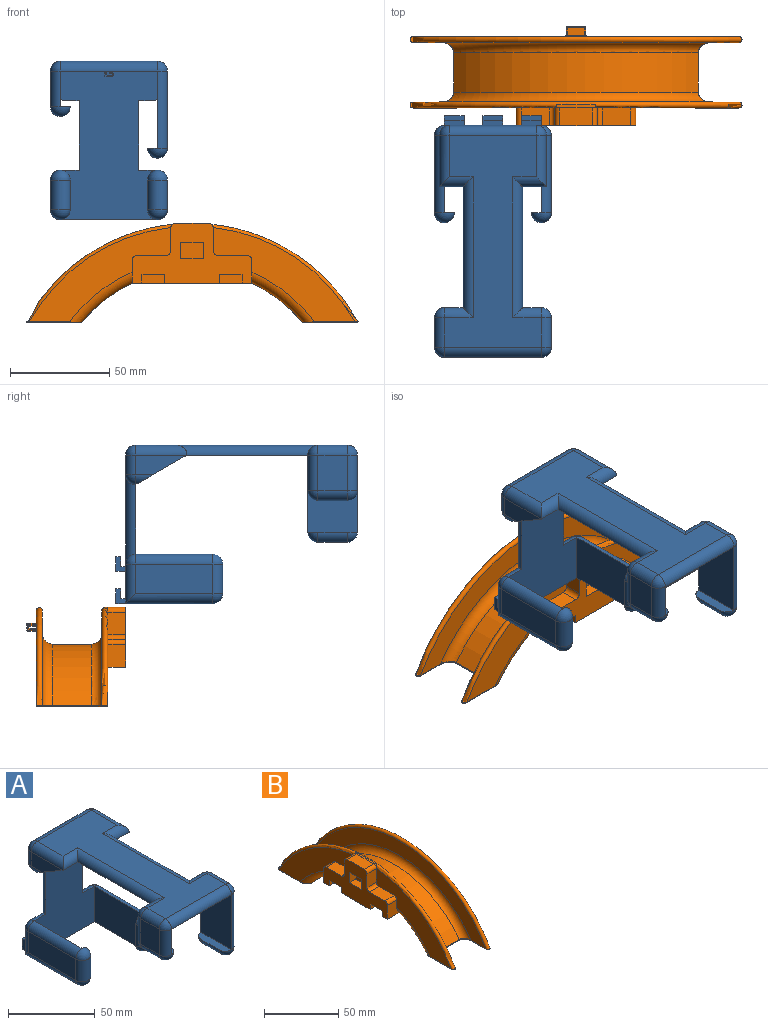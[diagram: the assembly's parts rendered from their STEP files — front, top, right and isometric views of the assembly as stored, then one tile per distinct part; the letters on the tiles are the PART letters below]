
ASSEMBLY  parts=2 mates=1
PART A: 174 faces, bbox 59x122x80 mm
  f0: plane 75x49mm, normal (0,-1,0), area 3005.6mm2, adj f8,f19,f20,f24,f27,f28,f47,f50
  f1: plane 10x2.5mm, normal (0,0,1), area 25mm2, adj f2,f87,f89,f95
  f2: plane 7.5x5mm, normal (1,0,0), area 25mm2, adj f1,f5,f88,f89,f94,f95
  f3: plane 10x2.5mm, normal (0,0,1), area 25mm2, adj f4,f81,f82,f93
  f4: plane 7.5x5mm, normal (1,0,0), area 25mm2, adj f3,f24,f38,f82,f92,f93
  f5: plane 75x49mm, normal (0,1,0), area 2245mm2, adj f2,f24,f38,f47,f50,f54,f61,f66
  f6: plane 25x5mm, normal (0,0,1), area 114.3mm2, adj f7,f15,f35,f41
  f7: plane 25x18mm, normal (1,0,0), area 450mm2, adj f6,f8,f46,f53
  f8: plane 112x49mm, normal (0,0,-1), area 4328.6mm2, adj f0,f7,f9,f27,f28,f45,f51,f56
  f9: plane 39x25mm, normal (-1,0,0), area 975mm2, adj f8,f10,f37,f43
  f10: plane 25x5mm, normal (0,0,1), area 114.3mm2, adj f9,f11,f32,f34
  f11: cylinder r=5mm len=15mm, axis (0,-1,0), area 235.6mm2, adj f10,f12,f32,f34
  f12: plane 39x15mm, normal (1,0,0), area 585mm2, adj f11,f37,f43,f44
  f13: plane 107x49mm, normal (0,0,1), area 3078.5mm2, adj f44,f45,f51,f52,f56,f59,f60,f62
  f14: plane 18x15mm, normal (-1,0,0), area 270mm2, adj f15,f46,f52,f53
  f15: cylinder r=5mm len=15mm, axis (0,-1,0), area 235.6mm2, adj f6,f14,f35,f41
  f16: plane 39x15mm, normal (1,0,0), area 585mm2, adj f17,f36,f38,f39
  f17: cylinder r=5mm len=15mm, axis (0,0,1), area 235.6mm2, adj f16,f18,f31,f33
  f18: plane 25x5mm, normal (0,1,0), area 114.3mm2, adj f17,f19,f31,f33
  f19: plane 39x25mm, normal (-1,0,0), area 975mm2, adj f0,f18,f36,f39
  f20: plane 39x25mm, normal (1,0,0), area 975mm2, adj f0,f21,f75,f79
  f21: plane 25x5mm, normal (0,1,0), area 114.3mm2, adj f20,f22,f73,f80
  f22: cylinder r=5mm len=15mm, axis (0,0,1), area 235.6mm2, adj f21,f23,f73,f80
  f23: plane 39x15mm, normal (-1,0,0), area 585mm2, adj f22,f75,f76,f79
  f24: plane 49x10mm, normal (0,0,-1), area 345mm2, adj f0,f4,f5,f36,f75,f81,f82,f83
  f25: plane 24.82x14.33mm, normal (0,-0.5,-0.87), area 65.4mm2, adj f26,f27,f55,f59
  f26: plane 25.98x10mm, normal (1,0,0), area 173.2mm2, adj f25,f55,f61,f62
  f27: plane 25.98x14.33mm, normal (-1,0,0), area 194.5mm2, adj f0,f8,f25,f55
  f28: plane 25.98x14.33mm, normal (1,0,0), area 194.5mm2, adj f0,f8,f29,f70
  f29: plane 24.82x14.33mm, normal (0,-0.5,-0.87), area 65.4mm2, adj f28,f30,f65,f70
  f30: plane 25.98x10mm, normal (-1,0,0), area 173.2mm2, adj f29,f67,f69,f70
  f31: sphere r=5mm, area 78.5mm2, adj f17,f18,f36
  f32: sphere r=5mm, area 78.5mm2, adj f10,f11,f37
  f33: sphere r=5mm, area 78.5mm2, adj f17,f18,f39
  f34: sphere r=5mm, area 78.5mm2, adj f10,f11,f43
  f35: sphere r=5mm, area 78.5mm2, adj f6,f15,f46
  f36: cylinder r=5mm len=44mm, axis (0,1,0), area 331.3mm2, adj f16,f19,f24,f31,f38
  f37: cylinder r=5mm len=39mm, axis (0,0,1), area 306.3mm2, adj f9,f12,f32,f40
  f38: cylinder r=5mm len=20mm, axis (0,0,-1), area 142.8mm2, adj f4,f5,f16,f36,f42
  f39: cylinder r=5mm len=39mm, axis (0,-1,0), area 306.3mm2, adj f16,f19,f33,f42
  f40: sphere r=5mm, area 39.3mm2, adj f37,f44,f45
  f41: sphere r=5mm, area 78.5mm2, adj f6,f15,f53
  f42: sphere r=5mm, area 39.3mm2, adj f38,f39,f47
  f43: cylinder r=5mm len=39mm, axis (0,0,-1), area 306.3mm2, adj f9,f12,f34,f48
  f44: cylinder r=5mm len=15mm, axis (0,-1,0), area 117.8mm2, adj f12,f13,f40,f48
  f45: cylinder r=5mm len=49mm, axis (-1,0,0), area 384.8mm2, adj f8,f13,f40,f49
  f46: cylinder r=5mm len=18mm, axis (0,0,-1), area 141.4mm2, adj f7,f14,f35,f49
  f47: cylinder r=5mm len=14.5mm, axis (-1,0,0), area 88.9mm2, adj f0,f5,f42,f50
  f48: sphere r=5mm, area 39.3mm2, adj f43,f44,f51
  f49: sphere r=5mm, area 39.3mm2, adj f45,f46,f52
  f50: cylinder r=5mm len=45mm, axis (0,0,1), area 303.4mm2, adj f0,f5,f47,f54
  f51: cylinder r=5mm len=14.5mm, axis (1,0,0), area 88.9mm2, adj f8,f13,f48,f56
  f52: cylinder r=5mm len=15mm, axis (0,-1,0), area 117.8mm2, adj f13,f14,f49,f57
  f53: cylinder r=5mm len=18mm, axis (0,0,1), area 141.4mm2, adj f7,f14,f41,f57
  f54: cylinder r=5mm len=12mm, axis (1,0,0), area 69.2mm2, adj f0,f5,f50,f58
  f55: cylinder r=5mm len=8.66mm, axis (0,-1,0), area 23.7mm2, adj f25,f26,f27,f58
  f56: cylinder r=5mm len=71.02mm, axis (0,-1,0), area 507.8mm2, adj f8,f13,f51,f59
  f57: sphere r=5mm, area 39.3mm2, adj f52,f53,f60
  f58: sphere r=5mm, area 39.3mm2, adj f0,f54,f55,f61
  f59: cylinder r=5mm len=17mm, axis (-1,0,0), area 94.2mm2, adj f8,f13,f25,f56,f62
  f60: cylinder r=5mm len=14.5mm, axis (1,0,0), area 88.9mm2, adj f8,f13,f57,f63
  f61: cylinder r=5mm len=10mm, axis (0,0,-1), area 78.5mm2, adj f5,f26,f58,f64
  f62: cylinder r=5mm len=25.98mm, axis (0,1,0), area 189.8mm2, adj f13,f26,f59,f64
  f63: cylinder r=5mm len=71.02mm, axis (0,1,0), area 507.8mm2, adj f8,f13,f60,f65
  f64: sphere r=5mm, area 39.3mm2, adj f61,f62,f66
  f65: cylinder r=5mm len=17mm, axis (1,0,0), area 94.2mm2, adj f8,f13,f29,f63,f67
  f66: cylinder r=5mm len=44mm, axis (-1,0,0), area 345.6mm2, adj f5,f13,f64,f68
  f67: cylinder r=5mm len=25.98mm, axis (0,1,0), area 189.8mm2, adj f13,f30,f65,f68
  f68: sphere r=5mm, area 39.3mm2, adj f66,f67,f69
  f69: cylinder r=5mm len=10mm, axis (0,0,-1), area 78.5mm2, adj f5,f30,f68,f71
  f70: cylinder r=5mm len=8.66mm, axis (0,-1,0), area 23.7mm2, adj f28,f29,f30,f71
  f71: sphere r=5mm, area 39.3mm2, adj f0,f69,f70,f72
  f72: cylinder r=5mm len=12mm, axis (-1,0,0), area 69.2mm2, adj f0,f5,f71,f74
  f73: sphere r=5mm, area 78.5mm2, adj f21,f22,f75
  f74: cylinder r=5mm len=45mm, axis (0,0,-1), area 303.4mm2, adj f0,f5,f72,f77
  f75: cylinder r=5mm len=44mm, axis (0,-1,0), area 331.3mm2, adj f20,f23,f24,f73,f76
  f76: cylinder r=5mm len=20mm, axis (0,0,1), area 142.8mm2, adj f5,f23,f75,f78,f83
  f77: cylinder r=5mm len=14.5mm, axis (-1,0,0), area 88.9mm2, adj f0,f5,f74,f78
  f78: sphere r=5mm, area 39.3mm2, adj f76,f77,f79
  f79: cylinder r=5mm len=39mm, axis (0,1,0), area 306.3mm2, adj f20,f23,f78,f80
  f80: sphere r=5mm, area 78.5mm2, adj f21,f22,f79
  f81: plane 7.5x5mm, normal (-1,0,0), area 25mm2, adj f3,f5,f24,f82,f92,f93
  f82: plane 10x7.5mm, normal (0,1,0), area 75mm2, adj f3,f4,f24,f81
  f83: plane 7.5x5mm, normal (-1,0,0), area 25mm2, adj f24,f76,f84,f86,f90,f91
  f84: plane 10x2.5mm, normal (0,0,1), area 25mm2, adj f83,f85,f86,f90
  f85: plane 7.5x5mm, normal (1,0,0), area 25mm2, adj f5,f24,f84,f86,f90,f91
  f86: plane 10x7.5mm, normal (0,1,0), area 75mm2, adj f24,f83,f84,f85
  f87: plane 7.5x5mm, normal (-1,0,0), area 25mm2, adj f1,f5,f88,f89,f94,f95
  f88: plane 10x5mm, normal (0,0,-1), area 50mm2, adj f2,f5,f87,f89
  f89: plane 10x7.5mm, normal (0,1,0), area 75mm2, adj f1,f2,f87,f88
  f90: plane 10x5mm, normal (0,-1,0), area 50mm2, adj f83,f84,f85,f91
  f91: plane 10x2.5mm, normal (0,0,1), area 25mm2, adj f5,f83,f85,f90
  f92: plane 10x2.5mm, normal (0,0,1), area 25mm2, adj f4,f5,f81,f93
  f93: plane 10x5mm, normal (0,-1,0), area 50mm2, adj f3,f4,f81,f92
  f94: plane 10x2.5mm, normal (0,0,1), area 25mm2, adj f2,f5,f87,f95
  f95: plane 10x5mm, normal (0,-1,0), area 50mm2, adj f1,f2,f87,f94
  f96: extruded ~0.75x0.41mm, area 0.3mm2, adj f0,f97,f117,f118
  f97: plane 0.75x0.15mm, normal (0,0,-1), area 0.1mm2, adj f0,f96,f98,f118
  f98: plane 0.75x0.23mm, normal (1,0,0), area 0.2mm2, adj f0,f97,f99,f118
  f99: plane 0.75x0.07mm, normal (0,0,1), area 0.1mm2, adj f0,f98,f100,f118
  f100: extruded ~0.75x0.35mm, area 0.3mm2, adj f0,f99,f101,f118
  f101: extruded ~0.75x0.22mm, area 0.2mm2, adj f0,f100,f102,f118
  f102: extruded ~0.75x0.21mm, area 0.2mm2, adj f0,f101,f103,f118
  f103: extruded ~0.75x0.23mm, area 0.2mm2, adj f0,f102,f104,f118
  f104: extruded ~0.75x0.57mm, area 0.4mm2, adj f0,f103,f105,f118
  f105: extruded ~0.75x0.44mm, area 0.4mm2, adj f0,f104,f106,f118
  f106: plane 0.75x0.2mm, normal (0,0,-1), area 0.1mm2, adj f0,f105,f107,f118
  f107: plane 0.75x0.22mm, normal (1,0,0), area 0.2mm2, adj f0,f106,f108,f118
  f108: plane 0.75x0.3mm, normal (0,0,1), area 0.2mm2, adj f0,f107,f109,f118
  f109: extruded ~0.75x0.11mm, area 0.1mm2, adj f0,f108,f110,f118
  f110: extruded ~0.75x0.16mm, area 0.1mm2, adj f0,f109,f111,f118
  f111: extruded ~0.75x0.18mm, area 0.2mm2, adj f0,f110,f112,f118
  f112: extruded ~0.75x0.17mm, area 0.2mm2, adj f0,f111,f113,f118
  f113: extruded ~0.75x0.27mm, area 0.2mm2, adj f0,f112,f114,f118
  f114: extruded ~0.75x0.39mm, area 0.3mm2, adj f0,f113,f115,f118
  f115: extruded ~0.75x0.32mm, area 0.2mm2, adj f0,f114,f116,f118
  f116: extruded ~0.75x0.28mm, area 0.3mm2, adj f0,f115,f117,f118
  f117: extruded ~0.75x0.29mm, area 0.3mm2, adj f0,f96,f116,f118
  f118: plane 1.86x1.09mm, normal (0,-1,0), area 0.8mm2, adj f96,f97,f98,f99,f100,f101,f102,f103
  f119: plane 0.75x0.3mm, normal (0,0,-1), area 0.2mm2, adj f0,f120,f122,f123
  f120: plane 1.86x0.75mm, normal (1,0,0), area 1.4mm2, adj f0,f119,f121,f123
  f121: plane 0.75x0.3mm, normal (0,0,1), area 0.2mm2, adj f0,f120,f122,f123
  f122: plane 1.86x0.75mm, normal (-1,0,0), area 1.4mm2, adj f0,f119,f121,f123
  f123: plane 1.86x0.3mm, normal (0,-1,0), area 0.6mm2, adj f119,f120,f121,f122
  f124: plane 1.45x0.75mm, normal (-1,0,0), area 1.1mm2, adj f0,f125,f141,f142
  f125: plane 0.75x0.31mm, normal (0,0,-1), area 0.2mm2, adj f0,f124,f126,f142
  f126: plane 1.42x0.75mm, normal (1,0,0), area 1.1mm2, adj f0,f125,f127,f142
  f127: extruded ~0.75x0.18mm, area 0.2mm2, adj f0,f126,f128,f142
  f128: extruded ~0.75x0.21mm, area 0.2mm2, adj f0,f127,f129,f142
  f129: extruded ~0.75x0.11mm, area 0.1mm2, adj f0,f128,f130,f142
  f130: extruded ~0.75x0.12mm, area 0.1mm2, adj f0,f129,f131,f142
  f131: extruded ~0.75x0.1mm, area 0.1mm2, adj f0,f130,f132,f142
  f132: extruded ~0.75x0.07mm, area 0.1mm2, adj f0,f131,f133,f142
  f133: plane 0.75x0.2mm, normal (0.85,0,-0.53), area 0.2mm2, adj f0,f132,f134,f142
  f134: extruded ~0.75x0.12mm, area 0.1mm2, adj f0,f133,f135,f142
  f135: extruded ~0.75x0.15mm, area 0.1mm2, adj f0,f134,f136,f142
  f136: extruded ~0.75x0.15mm, area 0.1mm2, adj f0,f135,f137,f142
  f137: extruded ~0.75x0.13mm, area 0.1mm2, adj f0,f136,f138,f142
  f138: extruded ~0.75x0.22mm, area 0.2mm2, adj f0,f137,f139,f142
  f139: extruded ~0.75x0.19mm, area 0.2mm2, adj f0,f138,f140,f142
  f140: extruded ~0.75x0.14mm, area 0.1mm2, adj f0,f139,f141,f142
  f141: extruded ~0.75x0.22mm, area 0.2mm2, adj f0,f124,f140,f142
  f142: plane 1.91x1.14mm, normal (0,-1,0), area 0.8mm2, adj f124,f125,f126,f127,f128,f129,f130,f131
  f143: plane 0.75x0.32mm, normal (0,0,1), area 0.2mm2, adj f0,f144,f167,f168
  f144: plane 0.75x0.73mm, normal (-0.87,0,-0.5), area 0.6mm2, adj f0,f143,f145,f168
  f145: extruded ~0.75x0.25mm, area 0.2mm2, adj f0,f144,f146,f168
  f146: extruded ~0.75x0.34mm, area 0.3mm2, adj f0,f145,f147,f168
  f147: extruded ~0.75x0.24mm, area 0.2mm2, adj f0,f146,f148,f168
  f148: extruded ~0.75x0.18mm, area 0.2mm2, adj f0,f147,f149,f168
  f149: extruded ~0.75x0.21mm, area 0.2mm2, adj f0,f148,f150,f168
  f150: extruded ~0.75x0.23mm, area 0.2mm2, adj f0,f149,f151,f168
  f151: plane 0.75x0.13mm, normal (0,0,-1), area 0.1mm2, adj f0,f150,f152,f168
  f152: plane 0.75x0.23mm, normal (1,0,0), area 0.2mm2, adj f0,f151,f153,f168
  f153: plane 0.75x0.12mm, normal (0,0,1), area 0.1mm2, adj f0,f152,f154,f168
  f154: extruded ~0.75x0.19mm, area 0.1mm2, adj f0,f153,f155,f168
  f155: extruded ~0.75x0.11mm, area 0.1mm2, adj f0,f154,f156,f168
  f156: extruded ~0.75x0.11mm, area 0.1mm2, adj f0,f155,f157,f168
  f157: extruded ~0.75x0.11mm, area 0.1mm2, adj f0,f156,f158,f168
  f158: extruded ~0.75x0.19mm, area 0.1mm2, adj f0,f157,f159,f168
  f159: extruded ~0.75x0.12mm, area 0.1mm2, adj f0,f158,f160,f168
  f160: extruded ~0.75x0.1mm, area 0.1mm2, adj f0,f159,f161,f168
  f161: extruded ~0.75x0.11mm, area 0.1mm2, adj f0,f160,f162,f168
  f162: plane 0.75x0.17mm, normal (0,0,-1), area 0.1mm2, adj f0,f161,f163,f168
  f163: plane 0.75x0.22mm, normal (1,0,0), area 0.2mm2, adj f0,f162,f164,f168
  f164: plane 0.75x0.14mm, normal (0,0,1), area 0.1mm2, adj f0,f163,f165,f168
  f165: extruded ~0.75x0.03mm, area 0mm2, adj f0,f164,f166,f168
  f166: extruded ~0.75x0.02mm, area 0mm2, adj f0,f165,f167,f168
  f167: plane 0.75x0.67mm, normal (0.89,0,0.46), area 0.6mm2, adj f0,f143,f166,f168
  f168: plane 1.86x0.85mm, normal (0,-1,0), area 0.7mm2, adj f143,f144,f145,f146,f147,f148,f149,f150
  f169: plane 0.75x0.3mm, normal (0,0,-1), area 0.2mm2, adj f0,f170,f172,f173
  f170: plane 1.86x0.75mm, normal (1,0,0), area 1.4mm2, adj f0,f169,f171,f173
  f171: plane 0.75x0.3mm, normal (0,0,1), area 0.2mm2, adj f0,f170,f172,f173
  f172: plane 1.86x0.75mm, normal (-1,0,0), area 1.4mm2, adj f0,f169,f171,f173
  f173: plane 1.86x0.3mm, normal (0,-1,0), area 0.6mm2, adj f169,f170,f171,f172
PART B: 213 faces, bbox 50x181.2x60.6 mm
  f0: plane 60.5x6.67mm, normal (1,0,0), area 268.3mm2, adj f14,f34,f54,f55,f56,f57,f58,f59
  f1: plane 9.75x0.5mm, normal (1,0,0), area 1.4mm2, adj f10,f39,f50
  f2: plane 9.75x0.5mm, normal (1,0,0), area 1.4mm2, adj f10,f39,f51
  f3: plane 9x6mm, normal (0,1,0), area 45mm2, adj f14,f15,f21,f24,f25,f28
  f4: plane 9x6mm, normal (0,1,0), area 45mm2, adj f5,f14,f21,f22,f23,f29
  f5: plane 11.5x4mm, normal (0,0,-1), area 46mm2, adj f4,f6,f23,f29
  f6: plane 9x6mm, normal (0,-1,0), area 45mm2, adj f5,f14,f21,f22,f23,f29
  f7: plane 14x11.5mm, normal (0,1,0), area 109.4mm2, adj f14,f21,f31,f34,f44,f48
  f8: plane 14.5x9mm, normal (0,0,1), area 130.5mm2, adj f21,f31,f48,f49
  f9: plane 11.25x9mm, normal (0,1,0), area 101.2mm2, adj f21,f31,f49,f50
  f10: plane 16.5x9mm, normal (0,0,1), area 148.5mm2, adj f1,f2,f21,f50,f51
  f11: plane 11.25x9mm, normal (0,-1,0), area 101.2mm2, adj f21,f32,f51,f52
  f12: plane 14.5x9mm, normal (0,0,1), area 130.5mm2, adj f21,f32,f52,f53
  f13: plane 14x11.5mm, normal (0,-1,0), area 109.4mm2, adj f14,f21,f32,f34,f43,f53
  f14: plane 60.5x9mm, normal (0,0,-1), area 406.5mm2, adj f0,f3,f4,f6,f7,f13,f20,f21
  f15: plane 11.5x4mm, normal (0,0,-1), area 46mm2, adj f3,f20,f25,f28
  f16: plane 13x6mm, normal (0,1,0), area 69mm2, adj f17,f19,f21,f26,f27,f30
  f17: plane 11.5x4mm, normal (0,0,-1), area 46mm2, adj f16,f18,f27,f30
  f18: plane 13x6mm, normal (0,-1,0), area 69mm2, adj f17,f19,f21,f26,f27,f30
  f19: plane 11.5x6mm, normal (0,0,1), area 69mm2, adj f16,f18,f21,f30
  f20: plane 9x6mm, normal (0,-1,0), area 45mm2, adj f14,f15,f21,f24,f25,f28
  f21: plane 60.5x30.25mm, normal (-1,0,0), area 992.4mm2, adj f3,f4,f6,f7,f8,f9,f10,f11
  f22: plane 11.5x2mm, normal (0,0,-1), area 23mm2, adj f4,f6,f21,f23
  f23: plane 11.5x4.5mm, normal (1,0,0), area 51.7mm2, adj f4,f5,f6,f22
  f24: plane 11.5x2mm, normal (0,0,-1), area 23mm2, adj f3,f20,f21,f25
  f25: plane 11.5x4.5mm, normal (1,0,0), area 51.7mm2, adj f3,f15,f20,f24
  f26: plane 11.5x2mm, normal (0,0,-1), area 23mm2, adj f16,f18,f21,f27
  f27: plane 11.5x4.5mm, normal (1,0,0), area 51.8mm2, adj f16,f17,f18,f26
  f28: plane 11.5x9mm, normal (-1,0,0), area 103.5mm2, adj f3,f14,f15,f20
  f29: plane 11.5x9mm, normal (-1,0,0), area 103.5mm2, adj f4,f5,f6,f14
  f30: plane 13x11.5mm, normal (-1,0,0), area 149.5mm2, adj f16,f17,f18,f19
  f31: plane 71.41x47.64mm, normal (-1,0,0), area 1179.6mm2, adj f7,f8,f9,f44,f46,f48,f49,f50
  f32: plane 71.41x47.64mm, normal (-1,0,0), area 1179.6mm2, adj f11,f12,f13,f43,f46,f51,f52,f53
  f33: plane 35x27.12mm, normal (0,0,-1), area 269.8mm2, adj f143,f144,f145,f146,f147,f148,f149,f150
  f34: cylinder r=71.94mm len=111.52mm, axis (-1,0,0), area 3629.9mm2, adj f0,f7,f13,f43,f44,f45,f146,f158
  f35: plane 35x27.12mm, normal (0,0,-1), area 269.8mm2, adj f155,f156,f157,f158,f159,f160,f161,f162
  f36: plane 164.26x48.25mm, normal (1,0,0), area 2882.5mm2, adj f45,f47,f143,f155,f175,f176,f182,f183
  f37: cylinder r=76.94mm len=123.25mm, axis (-1,0,0), area 2858.6mm2, adj f41,f42,f152,f163
  f38: plane 164.26x48.25mm, normal (-1,0,0), area 2175.8mm2, adj f42,f47,f148,f159
  f39: cylinder r=95.52mm len=19.5mm, axis (-1,0,0), area 29.3mm2, adj f1,f2,f46,f50,f51
  f40: plane 164.26x48.25mm, normal (1,0,0), area 2175.8mm2, adj f41,f46,f154,f166
  f41: torus R=81.94mm, axis (1,0,0), area 1172.3mm2, adj f37,f40,f153,f165
  f42: torus R=81.94mm, axis (1,0,0), area 1172.3mm2, adj f37,f38,f150,f161
  f43: torus R=76.94mm, axis (1,0,0), area 279.3mm2, adj f13,f32,f34,f147
  f44: torus R=76.94mm, axis (1,0,0), area 279.3mm2, adj f7,f31,f34,f160
  f45: torus R=76.94mm, axis (1,0,0), area 1048.2mm2, adj f34,f36,f144,f157
  f46: torus R=94.02mm, axis (1,0,0), area 906mm2, adj f31,f32,f39,f40,f50,f51,f151,f164
  f47: torus R=94.02mm, axis (1,0,0), area 954.3mm2, adj f36,f38,f145,f156
  f48: cylinder r=2.5mm len=9mm, axis (-1,0,0), area 35.3mm2, adj f7,f8,f21,f31
  f49: cylinder r=2.5mm len=9mm, axis (-1,0,0), area 35.3mm2, adj f8,f9,f21,f31
  f50: cylinder r=2.5mm len=10.5mm, axis (-1,0,0), area 36.1mm2, adj f1,f9,f10,f21,f31,f39,f46
  f51: cylinder r=2.5mm len=10.5mm, axis (1,0,0), area 36.1mm2, adj f2,f10,f11,f21,f32,f39,f46
  f52: cylinder r=2.5mm len=9mm, axis (-1,0,0), area 35.3mm2, adj f11,f12,f21,f32
  f53: cylinder r=2.5mm len=9mm, axis (-1,0,0), area 35.3mm2, adj f12,f13,f21,f32
  f54: extruded ~0.75x0.41mm, area 0.3mm2, adj f0,f55,f75,f76
  f55: plane 0.75x0.15mm, normal (0,0,-1), area 0.1mm2, adj f0,f54,f56,f76
  f56: plane 0.75x0.23mm, normal (0,1,0), area 0.2mm2, adj f0,f55,f57,f76
  f57: plane 0.75x0.07mm, normal (0,0,1), area 0.1mm2, adj f0,f56,f58,f76
  f58: extruded ~0.75x0.35mm, area 0.3mm2, adj f0,f57,f59,f76
  f59: extruded ~0.75x0.22mm, area 0.2mm2, adj f0,f58,f60,f76
  f60: extruded ~0.75x0.21mm, area 0.2mm2, adj f0,f59,f61,f76
  f61: extruded ~0.75x0.23mm, area 0.2mm2, adj f0,f60,f62,f76
  f62: extruded ~0.75x0.57mm, area 0.4mm2, adj f0,f61,f63,f76
  f63: extruded ~0.75x0.44mm, area 0.4mm2, adj f0,f62,f64,f76
  f64: plane 0.75x0.2mm, normal (0,0,-1), area 0.1mm2, adj f0,f63,f65,f76
  f65: plane 0.75x0.22mm, normal (0,1,0), area 0.2mm2, adj f0,f64,f66,f76
  f66: plane 0.75x0.3mm, normal (0,0,1), area 0.2mm2, adj f0,f65,f67,f76
  f67: extruded ~0.75x0.11mm, area 0.1mm2, adj f0,f66,f68,f76
  f68: extruded ~0.75x0.16mm, area 0.1mm2, adj f0,f67,f69,f76
  f69: extruded ~0.75x0.18mm, area 0.2mm2, adj f0,f68,f70,f76
  f70: extruded ~0.75x0.17mm, area 0.2mm2, adj f0,f69,f71,f76
  f71: extruded ~0.75x0.27mm, area 0.2mm2, adj f0,f70,f72,f76
  f72: extruded ~0.75x0.39mm, area 0.3mm2, adj f0,f71,f73,f76
  f73: extruded ~0.75x0.32mm, area 0.2mm2, adj f0,f72,f74,f76
  f74: extruded ~0.75x0.28mm, area 0.3mm2, adj f0,f73,f75,f76
  f75: extruded ~0.75x0.29mm, area 0.3mm2, adj f0,f54,f74,f76
  f76: plane 1.86x1.09mm, normal (1,0,0), area 0.8mm2, adj f54,f55,f56,f57,f58,f59,f60,f61
  f77: plane 0.75x0.3mm, normal (0,0,-1), area 0.2mm2, adj f0,f78,f80,f81
  f78: plane 1.86x0.75mm, normal (0,1,0), area 1.4mm2, adj f0,f77,f79,f81
  f79: plane 0.75x0.3mm, normal (0,0,1), area 0.2mm2, adj f0,f78,f80,f81
  f80: plane 1.86x0.75mm, normal (0,-1,0), area 1.4mm2, adj f0,f77,f79,f81
  f81: plane 1.86x0.3mm, normal (1,0,0), area 0.6mm2, adj f77,f78,f79,f80
  f82: plane 1.45x0.75mm, normal (0,-1,0), area 1.1mm2, adj f0,f83,f99,f100
  f83: plane 0.75x0.31mm, normal (0,0,-1), area 0.2mm2, adj f0,f82,f84,f100
  f84: plane 1.42x0.75mm, normal (0,1,0), area 1.1mm2, adj f0,f83,f85,f100
  f85: extruded ~0.75x0.18mm, area 0.2mm2, adj f0,f84,f86,f100
  f86: extruded ~0.75x0.21mm, area 0.2mm2, adj f0,f85,f87,f100
  f87: extruded ~0.75x0.11mm, area 0.1mm2, adj f0,f86,f88,f100
  f88: extruded ~0.75x0.12mm, area 0.1mm2, adj f0,f87,f89,f100
  f89: extruded ~0.75x0.1mm, area 0.1mm2, adj f0,f88,f90,f100
  f90: extruded ~0.75x0.07mm, area 0.1mm2, adj f0,f89,f91,f100
  f91: plane 0.75x0.2mm, normal (0,0.85,-0.53), area 0.2mm2, adj f0,f90,f92,f100
  f92: extruded ~0.75x0.12mm, area 0.1mm2, adj f0,f91,f93,f100
  f93: extruded ~0.75x0.15mm, area 0.1mm2, adj f0,f92,f94,f100
  f94: extruded ~0.75x0.15mm, area 0.1mm2, adj f0,f93,f95,f100
  f95: extruded ~0.75x0.13mm, area 0.1mm2, adj f0,f94,f96,f100
  f96: extruded ~0.75x0.22mm, area 0.2mm2, adj f0,f95,f97,f100
  f97: extruded ~0.75x0.19mm, area 0.2mm2, adj f0,f96,f98,f100
  f98: extruded ~0.75x0.14mm, area 0.1mm2, adj f0,f97,f99,f100
  f99: extruded ~0.75x0.22mm, area 0.2mm2, adj f0,f82,f98,f100
  f100: plane 1.91x1.14mm, normal (1,0,0), area 0.8mm2, adj f82,f83,f84,f85,f86,f87,f88,f89
  f101: plane 0.75x0.32mm, normal (0,0,1), area 0.2mm2, adj f0,f102,f125,f126
  f102: plane 0.75x0.73mm, normal (0,-0.87,-0.5), area 0.6mm2, adj f0,f101,f103,f126
  f103: extruded ~0.75x0.25mm, area 0.2mm2, adj f0,f102,f104,f126
  f104: extruded ~0.75x0.34mm, area 0.3mm2, adj f0,f103,f105,f126
  f105: extruded ~0.75x0.24mm, area 0.2mm2, adj f0,f104,f106,f126
  f106: extruded ~0.75x0.18mm, area 0.2mm2, adj f0,f105,f107,f126
  f107: extruded ~0.75x0.21mm, area 0.2mm2, adj f0,f106,f108,f126
  f108: extruded ~0.75x0.23mm, area 0.2mm2, adj f0,f107,f109,f126
  f109: plane 0.75x0.13mm, normal (0,0,-1), area 0.1mm2, adj f0,f108,f110,f126
  f110: plane 0.75x0.23mm, normal (0,1,0), area 0.2mm2, adj f0,f109,f111,f126
  f111: plane 0.75x0.12mm, normal (0,0,1), area 0.1mm2, adj f0,f110,f112,f126
  f112: extruded ~0.75x0.19mm, area 0.1mm2, adj f0,f111,f113,f126
  f113: extruded ~0.75x0.11mm, area 0.1mm2, adj f0,f112,f114,f126
  f114: extruded ~0.75x0.11mm, area 0.1mm2, adj f0,f113,f115,f126
  f115: extruded ~0.75x0.11mm, area 0.1mm2, adj f0,f114,f116,f126
  f116: extruded ~0.75x0.19mm, area 0.1mm2, adj f0,f115,f117,f126
  f117: extruded ~0.75x0.12mm, area 0.1mm2, adj f0,f116,f118,f126
  f118: extruded ~0.75x0.1mm, area 0.1mm2, adj f0,f117,f119,f126
  f119: extruded ~0.75x0.11mm, area 0.1mm2, adj f0,f118,f120,f126
  f120: plane 0.75x0.17mm, normal (0,0,-1), area 0.1mm2, adj f0,f119,f121,f126
  f121: plane 0.75x0.22mm, normal (0,1,0), area 0.2mm2, adj f0,f120,f122,f126
  f122: plane 0.75x0.14mm, normal (0,0,1), area 0.1mm2, adj f0,f121,f123,f126
  f123: extruded ~0.75x0.03mm, area 0mm2, adj f0,f122,f124,f126
  f124: extruded ~0.75x0.02mm, area 0mm2, adj f0,f123,f125,f126
  f125: plane 0.75x0.67mm, normal (0,0.89,0.46), area 0.6mm2, adj f0,f101,f124,f126
  f126: plane 1.86x0.85mm, normal (1,0,0), area 0.7mm2, adj f101,f102,f103,f104,f105,f106,f107,f108
  f127: plane 0.75x0.3mm, normal (0,0,-1), area 0.2mm2, adj f0,f128,f130,f131
  f128: plane 1.86x0.75mm, normal (0,1,0), area 1.4mm2, adj f0,f127,f129,f131
  f129: plane 0.75x0.3mm, normal (0,0,1), area 0.2mm2, adj f0,f128,f130,f131
  f130: plane 1.86x0.75mm, normal (0,-1,0), area 1.4mm2, adj f0,f127,f129,f131
  f131: plane 1.86x0.3mm, normal (1,0,0), area 0.6mm2, adj f127,f128,f129,f130
  f132: plane 4x0.5mm, normal (0,1,0), area 2mm2, adj f173,f174,f185,f186
  f133: plane 9x4mm, normal (0,0,1), area 36mm2, adj f167,f170,f174,f175
  f134: plane 4x0.5mm, normal (0,-1,0), area 2mm2, adj f170,f171,f183,f184
  f135: plane 9x4mm, normal (0,0,-1), area 36mm2, adj f172,f184,f185,f202
  f136: plane 9x0.5mm, normal (1,0,0), area 4.5mm2, adj f167,f171,f172,f173
  f137: plane 4x1mm, normal (0,1,0), area 2.1mm2, adj f180,f181,f195,f196,f197,f198
  f138: plane 9x3.3mm, normal (0,0,1), area 29.7mm2, adj f196,f202,f207,f211
  f139: plane 4x1mm, normal (0,-1,0), area 2.1mm2, adj f191,f200,f206,f208,f211,f212
  f140: plane 9x4mm, normal (0,0,-1), area 36mm2, adj f180,f187,f191,f192
  f141: plane 9x1mm, normal (1,0,0), area 9mm2, adj f181,f187,f199,f200
  f142: plane 9x0.2mm, normal (0,0,1), area 1.8mm2, adj f198,f199,f207,f208
  f143: cylinder r=0.5mm len=20.28mm, axis (0,-1,0), area 15.9mm2, adj f33,f36,f144,f145
  f144: bspline ~6.29x5.95mm, area 4.9mm2, adj f33,f45,f143,f146
  f145: bspline ~3.05x2.38mm, area 4.2mm2, adj f33,f47,f143,f148
  f146: cylinder r=0.5mm len=26mm, axis (-1,0,0), area 11.5mm2, adj f33,f34,f144,f147
  f147: bspline ~6.91x5.95mm, area 4.9mm2, adj f33,f43,f146,f149
  f148: cylinder r=0.5mm len=14.16mm, axis (0,1,0), area 11.1mm2, adj f33,f38,f145,f150
  f149: cylinder r=0.5mm len=20.28mm, axis (0,1,0), area 15.9mm2, adj f32,f33,f147,f151
  f150: bspline ~6.98x6.55mm, area 8.8mm2, adj f33,f42,f148,f152
  f151: bspline ~3.05x2.38mm, area 4.2mm2, adj f33,f46,f149,f154
  f152: cylinder r=0.5mm len=20mm, axis (-1,0,0), area 22.1mm2, adj f33,f37,f150,f153
  f153: bspline ~7.68x6.55mm, area 8.8mm2, adj f33,f41,f152,f154
  f154: cylinder r=0.5mm len=14.16mm, axis (0,-1,0), area 11.1mm2, adj f33,f40,f151,f153
  f155: cylinder r=0.5mm len=20.28mm, axis (0,-1,0), area 15.9mm2, adj f35,f36,f156,f157
  f156: bspline ~3.05x2.38mm, area 4.2mm2, adj f35,f47,f155,f159
  f157: bspline ~6.91x5.95mm, area 4.9mm2, adj f35,f45,f155,f158
  f158: cylinder r=0.5mm len=26mm, axis (-1,0,0), area 11.5mm2, adj f34,f35,f157,f160
  f159: cylinder r=0.5mm len=14.16mm, axis (0,1,0), area 11.1mm2, adj f35,f38,f156,f161
  f160: bspline ~6.29x5.95mm, area 4.9mm2, adj f35,f44,f158,f162
  f161: bspline ~7.68x6.55mm, area 8.8mm2, adj f35,f42,f159,f163
  f162: cylinder r=0.5mm len=20.28mm, axis (0,1,0), area 15.9mm2, adj f31,f35,f160,f164
  f163: cylinder r=0.5mm len=20mm, axis (-1,0,0), area 22.1mm2, adj f35,f37,f161,f165
  f164: bspline ~3.05x2.38mm, area 4.2mm2, adj f35,f46,f162,f166
  f165: bspline ~7.68x6.55mm, area 8.8mm2, adj f35,f41,f163,f166
  f166: cylinder r=0.5mm len=14.16mm, axis (0,-1,0), area 11.1mm2, adj f35,f40,f164,f165
  f167: cylinder r=0.5mm len=9mm, axis (0,1,0), area 7.1mm2, adj f133,f136,f168,f169
  f168: sphere r=0.5mm, area 0.4mm2, adj f167,f170,f171
  f169: sphere r=0.5mm, area 0.4mm2, adj f167,f173,f174
  f170: cylinder r=0.5mm len=4mm, axis (-1,0,0), area 3.1mm2, adj f133,f134,f168,f176
  f171: cylinder r=0.5mm len=0.5mm, axis (0,0,1), area 0.4mm2, adj f134,f136,f168,f177
  f172: cylinder r=0.5mm len=9mm, axis (0,-1,0), area 7.1mm2, adj f135,f136,f177,f178
  f173: cylinder r=0.5mm len=0.5mm, axis (0,0,-1), area 0.4mm2, adj f132,f136,f169,f178
  f174: cylinder r=0.5mm len=4mm, axis (1,0,0), area 3.1mm2, adj f132,f133,f169,f182
  f175: cylinder r=0.5mm len=9mm, axis (0,-1,0), area 7.1mm2, adj f36,f133,f176,f182
  f176: torus R=1mm, axis (1,0,0), area 0.8mm2, adj f36,f170,f175,f183
  f177: sphere r=0.5mm, area 0.4mm2, adj f171,f172,f184
  f178: sphere r=0.5mm, area 0.4mm2, adj f172,f173,f185
  f179: sphere r=0.5mm, area 0.4mm2, adj f180,f181,f187
  f180: cylinder r=0.5mm len=4mm, axis (-1,0,0), area 3.1mm2, adj f137,f140,f179,f188
  f181: cylinder r=0.5mm len=1mm, axis (0,0,-1), area 0.8mm2, adj f137,f141,f179,f189
  f182: torus R=1mm, axis (1,0,0), area 0.8mm2, adj f36,f174,f175,f186
  f183: cylinder r=0.5mm len=0.5mm, axis (0,0,-1), area 0.4mm2, adj f36,f134,f176,f193
  f184: cylinder r=0.5mm len=4mm, axis (1,0,0), area 3.1mm2, adj f134,f135,f177,f193
  f185: cylinder r=0.5mm len=4mm, axis (-1,0,0), area 3.1mm2, adj f132,f135,f178,f194
  f186: cylinder r=0.5mm len=0.5mm, axis (0,0,1), area 0.4mm2, adj f36,f132,f182,f194
  f187: cylinder r=0.5mm len=9mm, axis (0,-1,0), area 7.1mm2, adj f140,f141,f179,f190
  f188: torus R=1mm, axis (1,0,0), area 0.8mm2, adj f36,f180,f192,f195
  f189: sphere r=0.5mm, area 0.4mm2, adj f181,f198,f199
  f190: sphere r=0.5mm, area 0.4mm2, adj f187,f191,f200
  f191: cylinder r=0.5mm len=4mm, axis (1,0,0), area 3.1mm2, adj f139,f140,f190,f201
  f192: cylinder r=0.5mm len=9mm, axis (0,1,0), area 7.1mm2, adj f36,f140,f188,f201
  f193: torus R=1mm, axis (1,0,0), area 0.8mm2, adj f36,f183,f184,f202
  f194: torus R=1mm, axis (1,0,0), area 0.8mm2, adj f36,f185,f186,f202
  f195: cylinder r=0.5mm len=0.5mm, axis (0,0,1), area 0.4mm2, adj f36,f137,f188,f203
  f196: cylinder r=0.5mm len=3.8mm, axis (1,0,0), area 2.7mm2, adj f137,f138,f197,f203
  f197: cylinder r=0.5mm len=0.5mm, axis (0,0,-1), area 0.1mm2, adj f137,f196,f204
  f198: cylinder r=0.5mm len=0.5mm, axis (-1,0,0), area 0.2mm2, adj f137,f142,f189,f204
  f199: cylinder r=0.5mm len=9mm, axis (0,-1,0), area 7.1mm2, adj f141,f142,f189,f205
  f200: cylinder r=0.5mm len=1mm, axis (0,0,1), area 0.8mm2, adj f139,f141,f190,f205
  f201: torus R=1mm, axis (1,0,0), area 0.8mm2, adj f36,f191,f192,f206
  f202: cylinder r=0.5mm len=9mm, axis (0,1,0), area 14.1mm2, adj f135,f138,f193,f194,f203,f209
  f203: torus R=1mm, axis (1,0,0), area 0.8mm2, adj f36,f195,f196,f202
  f204: sphere r=0.5mm, area 0.4mm2, adj f197,f198,f207
  f205: sphere r=0.5mm, area 0.4mm2, adj f199,f200,f208
  f206: cylinder r=0.5mm len=0.5mm, axis (0,0,-1), area 0.4mm2, adj f36,f139,f201,f209
  f207: cylinder r=0.5mm len=9mm, axis (0,1,0), area 7.1mm2, adj f138,f142,f204,f210
  f208: cylinder r=0.5mm len=0.5mm, axis (1,0,0), area 0.2mm2, adj f139,f142,f205,f210
  f209: torus R=1mm, axis (1,0,0), area 0.8mm2, adj f36,f202,f206,f211
  f210: sphere r=0.5mm, area 0.4mm2, adj f207,f208,f212
  f211: cylinder r=0.5mm len=3.8mm, axis (-1,0,0), area 2.7mm2, adj f138,f139,f209,f212
  f212: cylinder r=0.5mm len=0.5mm, axis (0,0,1), area 0.1mm2, adj f139,f210,f211
PLACE A t=(-25.73,-151.11,34.92)mm
PLACE B rot(axis=(0,0,1),90deg) t=(-12.91,-34.11,-52.7)mm
MATE planar B.f21 <-> A.f5  axis (0,-1,0) through (18.83,-34.11,-24.05)mm
